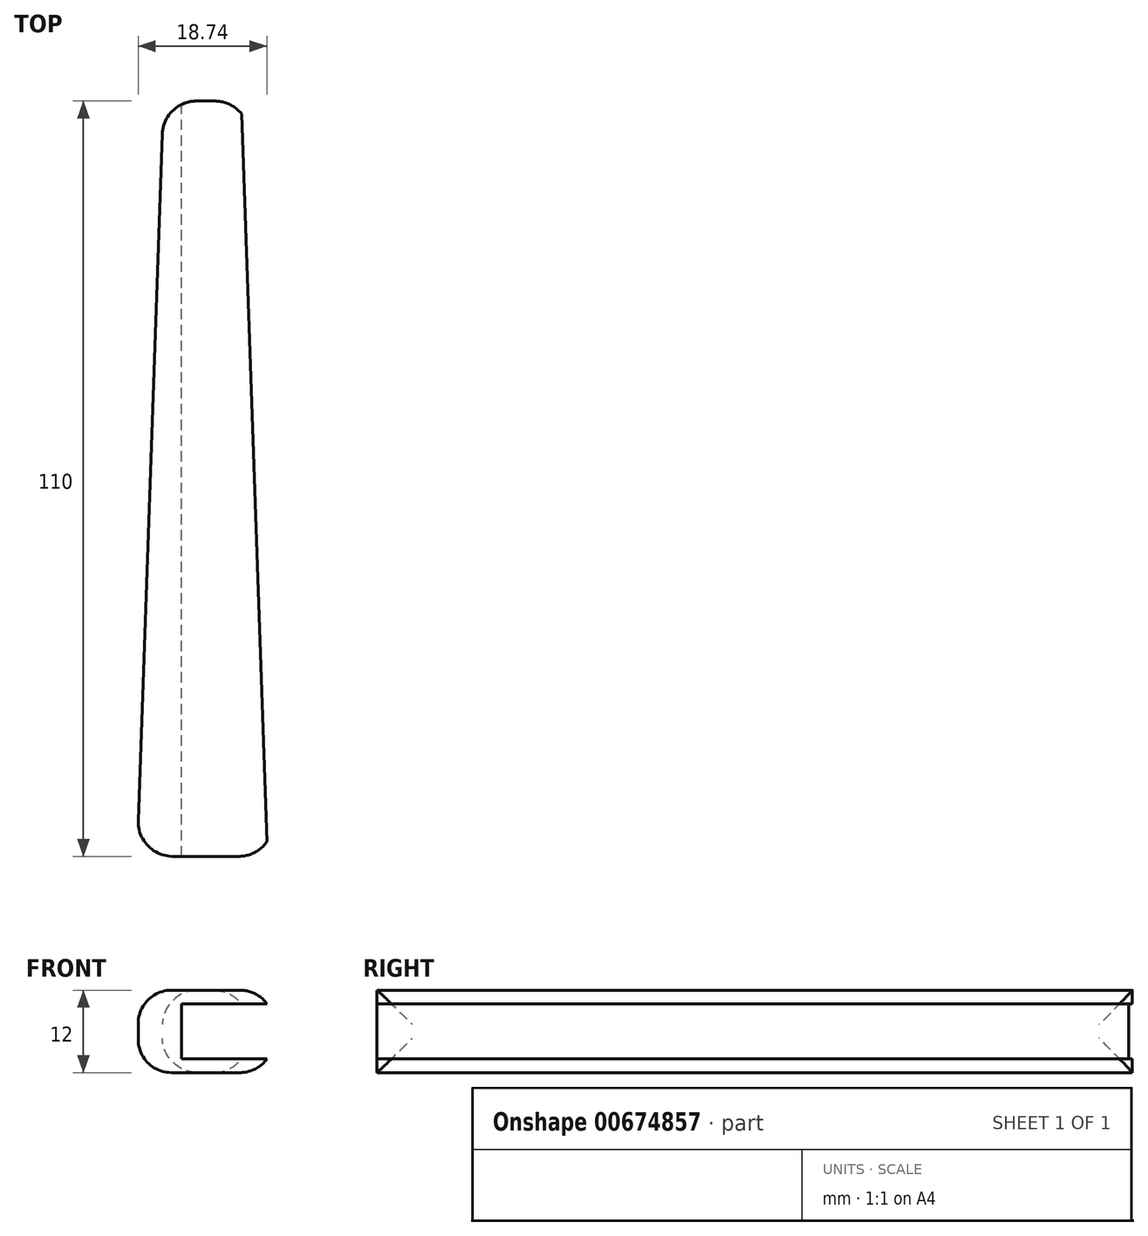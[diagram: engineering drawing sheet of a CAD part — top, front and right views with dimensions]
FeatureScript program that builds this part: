
annotation { "Feature Type Name" : "Feature", "Feature Type Description" : "" }
export const myFeature = defineFeature(function(context is Context, id is Id, definition is map)
    precondition{}
    {
        {
            var Q0;
            Q0=qCreatedBy(makeId("Top.planeOp"),FACE);
            var sketch = newSketch(context, id + "F0", { "sketchPlane" : qUnion([Q0])});
            skLineSegment(sketch, "E0.bottom", {"start": v(10, -55) * mm, "end": v(-10, -55) * mm});
            skLineSegment(sketch, "E0.top", {"start": v(10, 55) * mm, "end": v(-10, 55) * mm});
            skLineSegment(sketch, "E0.left", {"start": v(10, -55) * mm, "end": v(10, 55) * mm});
            skLineSegment(sketch, "E0.right", {"start": v(-10, -55) * mm, "end": v(-10, 55) * mm});
            skPoint(sketch, "E0.middle", {"position": v(0, 0) * mm});
            skSolve(sketch);
        }
        {
            var Q0;
            Q0=makeQuery(id+"F0.imprint","IMPRINT",FACE,{"disambiguationData":[TD([[makeQuery(id+"F0.imprint","IMPRINT",EDGE,{"derivedFrom":sQuery(id+"F0.wireOp",EDGE,"E0.bottom")}),-1.0]])]});
            extrude(context, id + "F1", {"entities" : qUnion([Q0]), "depth" : 12 * mm, "offsetDistance" : 25 * mm});
        }
        {
            var Q0;
            Q0=makeQuery(id+"F1.opExtrude","CAP_FACE",FACE,{"disambiguationData":[OSD([sQuery(id+"F0.wireOp",EDGE,"E0.bottom"),sQuery(id+"F0.wireOp",EDGE,"E0.top"),sQuery(id+"F0.wireOp",EDGE,"E0.left"),sQuery(id+"F0.wireOp",EDGE,"E0.right")])],"isStart":false});
            var sketch = newSketch(context, id + "F2", { "sketchPlane" : qUnion([Q0])});
            skLineSegment(sketch, "E1", {"start": v(-10, -55) * mm, "end": v(-6.16, 55) * mm});
            skLineSegment(sketch, "E2", {"start": v(-6.16, 55) * mm, "end": v(6.16, 55) * mm});
            skLineSegment(sketch, "E3", {"start": v(6.16, 55) * mm, "end": v(10, -55) * mm});
            skLineSegment(sketch, "E4", {"start": v(10, -55) * mm, "end": v(-10, -55) * mm});
            skSolve(sketch);
        }
        {
            var Q0;
            {var subQ0=sQuery(id+"F2.wireOp",EDGE,"E3");Q0=makeQuery(id+"F2.imprint","IMPRINT",FACE,{"disambiguationData":[TD([[makeQuery(id+"F2.imprint","IMPRINT",EDGE,{"derivedFrom":subQ0}),1.0]])]});}
            var Q1;
            {var subQ0=sQuery(id+"F2.wireOp",EDGE,"E1");Q1=makeQuery(id+"F2.imprint","IMPRINT",FACE,{"disambiguationData":[TD([[makeQuery(id+"F2.imprint","IMPRINT",EDGE,{"derivedFrom":subQ0}),1.0]])]});}
            extrude(context, id + "F3", {"entities" : qUnion([Q0, Q1]), "operationType" : NewBodyOperationType.REMOVE, "endBound" : BoundingType.THROUGH_ALL, "oppositeDirection" : true, "depth" : 25 * mm, "offsetDistance" : 25 * mm});
        }
        {
            var Q0;
            Q0=makeQuery(id+"F3.boolean.opBoolean","COPY",FACE,{"derivedFrom":makeQuery(id+"F3.opExtrude","SWEPT_FACE",FACE,{"disambiguationData":[OSD([sQuery(id+"F2.wireOp",EDGE,"E3")])]})});
            fillet(context, id + "F4", {"entities" : qUnion([Q0]), "radius" : 5 * mm, "tangentPropagation" : true, "allowEdgeOverflow" : false});
        }
        {
            var Q0;
            Q0=makeQuery(id+"F3.boolean.opBoolean","COPY",FACE,{"derivedFrom":makeQuery(id+"F3.opExtrude","SWEPT_FACE",FACE,{"disambiguationData":[OSD([sQuery(id+"F2.wireOp",EDGE,"E1")])]})});
            fillet(context, id + "F5", {"entities" : qUnion([Q0]), "radius" : 5 * mm, "tangentPropagation" : true, "allowEdgeOverflow" : false});
        }
        {
            var Q0;
            Q0=makeQuery(id+"F1.opExtrude","SWEPT_FACE",FACE,{"disambiguationData":[OSD([sQuery(id+"F0.wireOp",EDGE,"E0.top")])]});
            var sketch = newSketch(context, id + "F6", { "sketchPlane" : qUnion([Q0])});
            skPoint(sketch, "E5.firstSnap0", {"position": v(1.16, 2) * mm});
            skPoint(sketch, "E5.oppositeSnap0", {"position": v(1.16, 10) * mm});
            skLineSegment(sketch, "E5.bottom", {"start": v(3.5, 2) * mm, "end": v(-10.37, 2) * mm});
            skLineSegment(sketch, "E5.top", {"start": v(3.5, 10) * mm, "end": v(-10.37, 10) * mm});
            skLineSegment(sketch, "E5.left", {"start": v(3.5, 2) * mm, "end": v(3.5, 10) * mm});
            skLineSegment(sketch, "E5.right", {"start": v(-10.37, 2) * mm, "end": v(-10.37, 10) * mm});
            skSolve(sketch);
        }
        {
            var Q0;
            {var subQ0=sQuery(id+"F6.wireOp",EDGE,"E5.right");Q0=makeQuery(id+"F6.imprint","IMPRINT",FACE,{"disambiguationData":[TD([[makeQuery(id+"F6.imprint","IMPRINT",EDGE,{"derivedFrom":subQ0}),-1.0]])]});}
            var Q1;
            {var subQ0=sQuery(id+"F6.wireOp",EDGE,"E5.bottom");var subQ1=sQuery(id+"F0.wireOp",EDGE,"E0.top");var subQ2=makeQuery(id+"F1.opExtrude","SWEPT_FACE",FACE,{"disambiguationData":[OSD([subQ1])]});var subQ3=sQuery(id+"F2.wireOp",EDGE,"E2");var subQ4=makeQuery(id+"F5.opFillet","BLEND_EDGE",EDGE,{"blendedFrom":[makeQuery(id+"F3.boolean.opBoolean","COPY",EDGE,{"derivedFrom":makeQuery(id+"F3.opExtrude","SWEPT_EDGE",EDGE,{"disambiguationData":[OSD([subQ1,sQuery(id+"F2.wireOp",EDGE,"E1"),subQ3])]})}),subQ2],"blendedInto":[subQ2]});var subQ5=makeQuery(id+"F6.imprint","INTERSECT",VERTEX,{"derivedFrom":[subQ4,subQ0]});Q1=makeQuery(id+"F6.imprint","IMPRINT",FACE,{"disambiguationData":[TD([[makeQuery(id+"F6.imprint","IMPRINT",EDGE,{"disambiguationData":[TD([[subQ5,-1.0]])],"derivedFrom":subQ0}),-1.0]])]});}
            var Q2;
            {var subQ0=sQuery(id+"F6.wireOp",EDGE,"E5.left");Q2=makeQuery(id+"F6.imprint","IMPRINT",FACE,{"disambiguationData":[TD([[makeQuery(id+"F6.imprint","IMPRINT",EDGE,{"derivedFrom":subQ0}),1.0]])]});}
            extrude(context, id + "F7", {"entities" : qUnion([Q0, Q1, Q2]), "operationType" : NewBodyOperationType.REMOVE, "endBound" : BoundingType.THROUGH_ALL, "oppositeDirection" : true, "depth" : 25 * mm, "offsetDistance" : 25 * mm});
        }
    });
